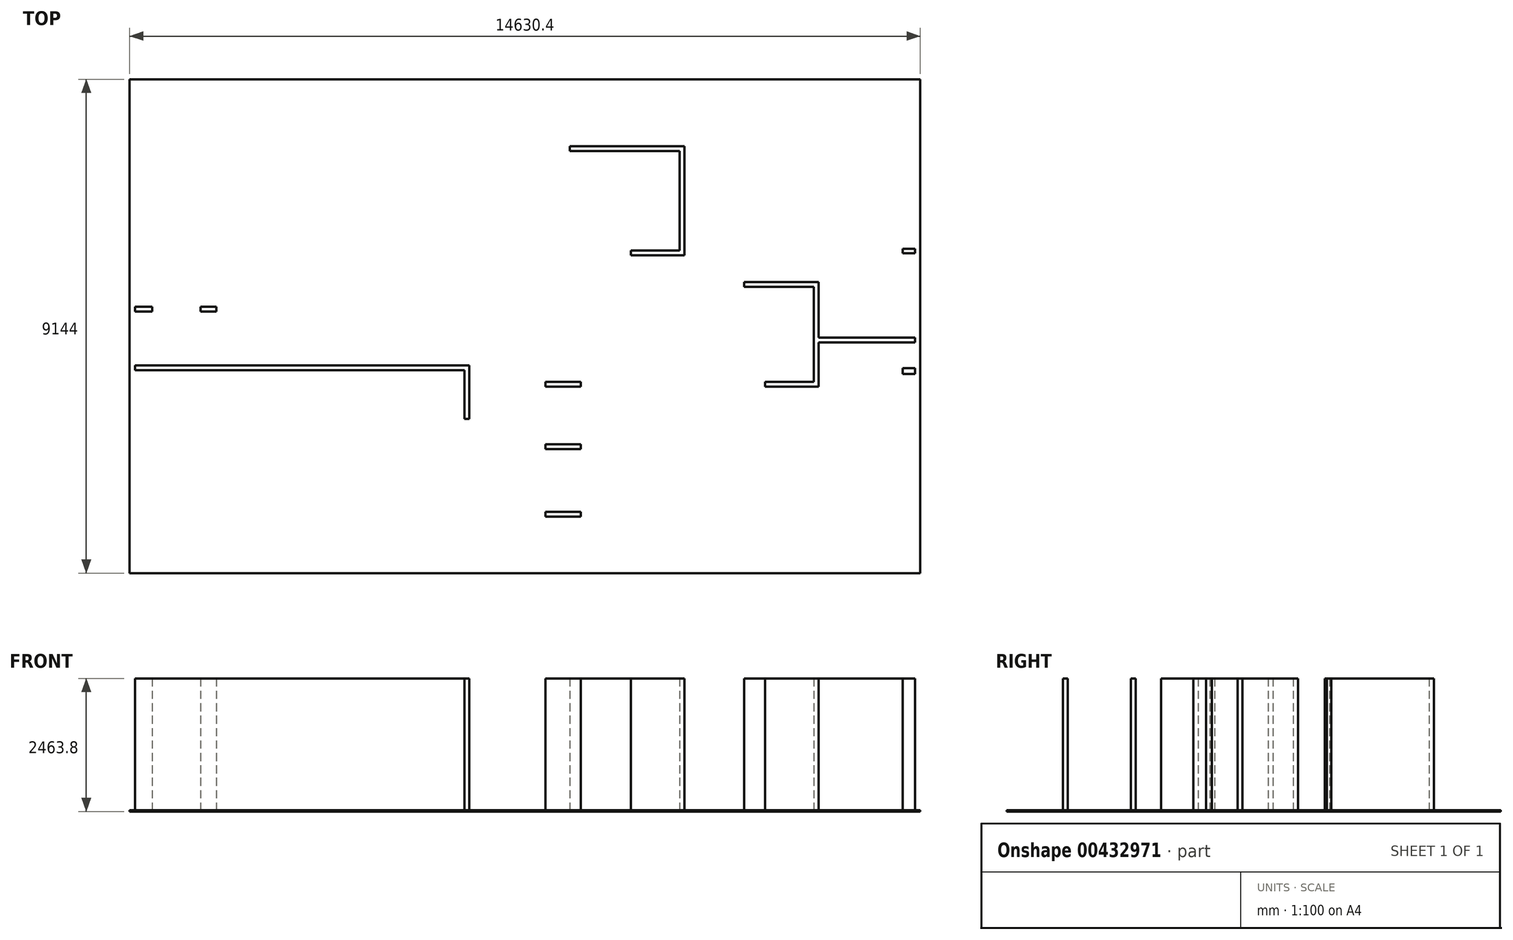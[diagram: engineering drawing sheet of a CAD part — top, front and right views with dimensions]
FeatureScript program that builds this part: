
annotation { "Feature Type Name" : "Feature", "Feature Type Description" : "" }
export const myFeature = defineFeature(function(context is Context, id is Id, definition is map)
    precondition{}
    {
        {
            var Q0;
            Q0=qCreatedBy(makeId("Top.planeOp"),FACE);
            var sketch = newSketch(context, id + "F0", { "sketchPlane" : qUnion([Q0])});
            skLineSegment(sketch, "E0.bottom", {"start": v(-7315.2, -4572) * mm, "end": v(7315.2, -4572) * mm});
            skLineSegment(sketch, "E0.top", {"start": v(-7315.2, 4572) * mm, "end": v(7315.2, 4572) * mm});
            skLineSegment(sketch, "E0.left", {"start": v(-7315.2, -4572) * mm, "end": v(-7315.2, 4572) * mm});
            skLineSegment(sketch, "E0.right", {"start": v(7315.2, -4572) * mm, "end": v(7315.2, 4572) * mm});
            skPoint(sketch, "E0.middle", {"position": v(0, 0) * mm});
            skSolve(sketch);
        }
        {
            var Q0;
            Q0 = qSketchRegion(id + "F0", true);
            extrude(context, id + "F1", {"entities" : qUnion([Q0]), "depth" : 25.4 * mm});
        }
        {
            var Q0;
            Q0=makeQuery(id+"F1.opExtrude","CAP_FACE",FACE,{"disambiguationData":[OSD([sQuery(id+"F0.wireOp",EDGE,"E0.bottom"),sQuery(id+"F0.wireOp",EDGE,"E0.top"),sQuery(id+"F0.wireOp",EDGE,"E0.left"),sQuery(id+"F0.wireOp",EDGE,"E0.right")])],"isStart":false});
            var sketch = newSketch(context, id + "F2", { "sketchPlane" : qUnion([Q0])});
            skLineSegment(sketch, "E1.0", {"start": v(-7216.78, 4473.58) * mm, "end": v(7216.77, 4473.58) * mm});
            skLineSegment(sketch, "E1.1", {"start": v(-7216.78, -4473.58) * mm, "end": v(-7216.78, 4473.58) * mm});
            skLineSegment(sketch, "E1.2", {"start": v(-7216.78, -4473.58) * mm, "end": v(7216.78, -4473.58) * mm});
            skLineSegment(sketch, "E1.3", {"start": v(7216.78, -4473.58) * mm, "end": v(7216.77, 4473.58) * mm});
            skLineSegment(sketch, "E2.bottom", {"start": v(-7216.78, -815.98) * mm, "end": v(-1120.78, -815.98) * mm});
            skLineSegment(sketch, "E2.top", {"start": v(-7216.78, -727.08) * mm, "end": v(-1120.78, -727.08) * mm});
            skLineSegment(sketch, "E2.left", {"start": v(-7216.78, -815.98) * mm, "end": v(-7216.78, -727.08) * mm});
            skLineSegment(sketch, "E2.right", {"start": v(-1120.78, -815.98) * mm, "end": v(-1120.78, -727.08) * mm});
            skLineSegment(sketch, "E3.bottom", {"start": v(-1120.78, -727.08) * mm, "end": v(-1031.88, -727.08) * mm});
            skLineSegment(sketch, "E3.top", {"start": v(-1120.78, -1715.42) * mm, "end": v(-1031.87, -1715.42) * mm});
            skLineSegment(sketch, "E3.left", {"start": v(-1120.78, -727.08) * mm, "end": v(-1120.78, -1715.42) * mm});
            skLineSegment(sketch, "E3.right", {"start": v(-1031.88, -727.08) * mm, "end": v(-1031.87, -1715.42) * mm});
            skLineSegment(sketch, "E4.bottom", {"start": v(-1031.87, -4473.58) * mm, "end": v(-1120.77, -4473.58) * mm});
            skLineSegment(sketch, "E4.top", {"start": v(-1031.87, -2919.2) * mm, "end": v(-1120.78, -2919.2) * mm});
            skLineSegment(sketch, "E4.left", {"start": v(-1031.87, -4473.58) * mm, "end": v(-1031.87, -2919.2) * mm});
            skLineSegment(sketch, "E4.right", {"start": v(-1120.77, -4473.58) * mm, "end": v(-1120.78, -2919.2) * mm});
            skLineSegment(sketch, "E5.bottom", {"start": v(-7216.78, 356.82) * mm, "end": v(-6898.68, 356.82) * mm});
            skLineSegment(sketch, "E5.top", {"start": v(-7216.78, 267.92) * mm, "end": v(-6898.68, 267.92) * mm});
            skLineSegment(sketch, "E5.left", {"start": v(-7216.78, 356.82) * mm, "end": v(-7216.78, 267.92) * mm});
            skLineSegment(sketch, "E5.right", {"start": v(-6898.68, 356.82) * mm, "end": v(-6898.68, 267.92) * mm});
            skLineSegment(sketch, "E6.bottom", {"start": v(-6003.33, 356.82) * mm, "end": v(-5713.3, 356.82) * mm});
            skLineSegment(sketch, "E6.top", {"start": v(-6003.33, 267.92) * mm, "end": v(-5713.3, 267.92) * mm});
            skLineSegment(sketch, "E6.left", {"start": v(-6003.33, 356.82) * mm, "end": v(-6003.33, 267.92) * mm});
            skLineSegment(sketch, "E6.right", {"start": v(-5713.3, 356.82) * mm, "end": v(-5713.3, 267.92) * mm});
            skLineSegment(sketch, "E7.bottom", {"start": v(-5864.23, -727.08) * mm, "end": v(-5775.33, -727.08) * mm});
            skLineSegment(sketch, "E7.top", {"start": v(-5864.23, 267.92) * mm, "end": v(-5775.33, 267.92) * mm});
            skLineSegment(sketch, "E7.left", {"start": v(-5864.23, -727.08) * mm, "end": v(-5864.23, 267.92) * mm});
            skLineSegment(sketch, "E7.right", {"start": v(-5775.33, -727.08) * mm, "end": v(-5775.33, 267.92) * mm});
            skLineSegment(sketch, "E8.bottom", {"start": v(-3994.28, -727.08) * mm, "end": v(-3905.38, -727.08) * mm});
            skLineSegment(sketch, "E8.top", {"start": v(-3994.28, 202.17) * mm, "end": v(-3905.38, 202.17) * mm});
            skLineSegment(sketch, "E8.left", {"start": v(-3994.28, -727.08) * mm, "end": v(-3994.28, 202.17) * mm});
            skLineSegment(sketch, "E8.right", {"start": v(-3905.38, -727.08) * mm, "end": v(-3905.38, 202.17) * mm});
            skLineSegment(sketch, "E9.bottom", {"start": v(1031.88, -4473.58) * mm, "end": v(942.97, -4473.58) * mm});
            skLineSegment(sketch, "E9.top", {"start": v(1031.88, -3530.3) * mm, "end": v(942.97, -3530.3) * mm});
            skLineSegment(sketch, "E9.left", {"start": v(1031.88, -4473.58) * mm, "end": v(1031.88, -3530.3) * mm});
            skLineSegment(sketch, "E9.right", {"start": v(942.97, -4473.58) * mm, "end": v(942.97, -3530.3) * mm});
            skLineSegment(sketch, "E10.bottom", {"start": v(1031.88, -3530.3) * mm, "end": v(380.54, -3530.3) * mm});
            skLineSegment(sketch, "E10.top", {"start": v(1031.88, -3441.4) * mm, "end": v(380.54, -3441.4) * mm});
            skLineSegment(sketch, "E10.left", {"start": v(1031.88, -3530.3) * mm, "end": v(1031.88, -3441.4) * mm});
            skLineSegment(sketch, "E10.right", {"start": v(380.54, -3530.3) * mm, "end": v(380.54, -3441.4) * mm});
            skLineSegment(sketch, "E11.bottom", {"start": v(4168.78, -4473.58) * mm, "end": v(4079.87, -4473.58) * mm});
            skLineSegment(sketch, "E11.top", {"start": v(4168.78, -1279.36) * mm, "end": v(4079.87, -1279.36) * mm});
            skLineSegment(sketch, "E11.left", {"start": v(4168.78, -4473.58) * mm, "end": v(4168.78, -1279.36) * mm});
            skLineSegment(sketch, "E11.right", {"start": v(4079.87, -4473.58) * mm, "end": v(4079.87, -1279.36) * mm});
            skLineSegment(sketch, "E12", {"start": v(0, -4473.58) * mm, "end": v(0, 0) * mm, "construction": true});
            skLineSegment(sketch, "E13.bottom", {"start": v(1031.88, -3441.4) * mm, "end": v(942.97, -3441.4) * mm});
            skLineSegment(sketch, "E13.top", {"start": v(1031.87, -2277.18) * mm, "end": v(942.97, -2277.18) * mm});
            skLineSegment(sketch, "E13.left", {"start": v(1031.88, -3441.4) * mm, "end": v(1031.88, -2277.18) * mm});
            skLineSegment(sketch, "E13.right", {"start": v(942.97, -3441.4) * mm, "end": v(942.97, -2277.18) * mm});
            skLineSegment(sketch, "E14.bottom", {"start": v(1031.87, -2277.18) * mm, "end": v(380.54, -2277.18) * mm});
            skLineSegment(sketch, "E14.top", {"start": v(1031.87, -2188.28) * mm, "end": v(380.54, -2188.28) * mm});
            skLineSegment(sketch, "E14.left", {"start": v(1031.87, -2277.18) * mm, "end": v(1031.87, -2188.28) * mm});
            skLineSegment(sketch, "E14.right", {"start": v(380.54, -2277.18) * mm, "end": v(380.54, -2188.28) * mm});
            skLineSegment(sketch, "E15.bottom", {"start": v(380.54, -2188.28) * mm, "end": v(458.38, -2188.28) * mm});
            skLineSegment(sketch, "E15.top", {"start": v(380.54, -1120.78) * mm, "end": v(458.38, -1120.78) * mm});
            skLineSegment(sketch, "E15.left", {"start": v(380.54, -2188.28) * mm, "end": v(380.54, -1120.78) * mm});
            skLineSegment(sketch, "E15.right", {"start": v(458.38, -2188.28) * mm, "end": v(458.38, -1120.78) * mm});
            skLineSegment(sketch, "E16.bottom", {"start": v(380.54, -1120.78) * mm, "end": v(1031.88, -1120.78) * mm});
            skLineSegment(sketch, "E16.top", {"start": v(380.54, -1031.87) * mm, "end": v(1031.88, -1031.87) * mm});
            skLineSegment(sketch, "E16.left", {"start": v(380.54, -1120.78) * mm, "end": v(380.54, -1031.87) * mm});
            skLineSegment(sketch, "E16.right", {"start": v(1031.88, -1120.78) * mm, "end": v(1031.88, -1031.87) * mm});
            skLineSegment(sketch, "E17.bottom", {"start": v(7216.78, 1432.79) * mm, "end": v(6987.65, 1432.79) * mm});
            skLineSegment(sketch, "E17.top", {"start": v(7216.78, 1350.5) * mm, "end": v(6987.65, 1350.5) * mm});
            skLineSegment(sketch, "E17.left", {"start": v(7216.78, 1432.79) * mm, "end": v(7216.78, 1350.5) * mm});
            skLineSegment(sketch, "E17.right", {"start": v(6987.65, 1432.79) * mm, "end": v(6987.65, 1350.5) * mm});
            skLineSegment(sketch, "E18.bottom", {"start": v(7216.78, -777.08) * mm, "end": v(6987.65, -777.08) * mm});
            skLineSegment(sketch, "E18.top", {"start": v(7216.78, -884.11) * mm, "end": v(6987.65, -884.11) * mm});
            skLineSegment(sketch, "E18.left", {"start": v(7216.78, -777.08) * mm, "end": v(7216.78, -884.11) * mm});
            skLineSegment(sketch, "E18.right", {"start": v(6987.65, -777.08) * mm, "end": v(6987.65, -884.11) * mm});
            skLineSegment(sketch, "E19.bottom", {"start": v(7216.78, -209.65) * mm, "end": v(5437.04, -209.65) * mm});
            skLineSegment(sketch, "E19.top", {"start": v(7216.78, -298.55) * mm, "end": v(5437.04, -298.55) * mm});
            skLineSegment(sketch, "E19.left", {"start": v(7216.78, -209.65) * mm, "end": v(7216.78, -298.55) * mm});
            skLineSegment(sketch, "E19.right", {"start": v(5437.04, -209.65) * mm, "end": v(5437.04, -298.55) * mm});
            skLineSegment(sketch, "E20.bottom", {"start": v(5348.14, 815.98) * mm, "end": v(5437.04, 815.98) * mm});
            skLineSegment(sketch, "E20.top", {"start": v(5348.14, -1120.77) * mm, "end": v(5437.04, -1120.77) * mm});
            skLineSegment(sketch, "E20.left", {"start": v(5348.14, 815.98) * mm, "end": v(5348.14, -1120.77) * mm});
            skLineSegment(sketch, "E20.right", {"start": v(5437.04, 815.98) * mm, "end": v(5437.04, -1120.77) * mm});
            skLineSegment(sketch, "E21.bottom", {"start": v(5348.14, -1120.77) * mm, "end": v(4444.86, -1120.77) * mm});
            skLineSegment(sketch, "E21.top", {"start": v(5348.14, -1031.87) * mm, "end": v(4444.86, -1031.87) * mm});
            skLineSegment(sketch, "E21.left", {"start": v(5348.14, -1120.77) * mm, "end": v(5348.14, -1031.87) * mm});
            skLineSegment(sketch, "E21.right", {"start": v(4444.86, -1120.77) * mm, "end": v(4444.86, -1031.87) * mm});
            skLineSegment(sketch, "E22.bottom", {"start": v(5348.14, 815.98) * mm, "end": v(4058.9, 815.98) * mm});
            skLineSegment(sketch, "E22.top", {"start": v(5348.14, 727.08) * mm, "end": v(4058.9, 727.08) * mm});
            skLineSegment(sketch, "E22.left", {"start": v(5348.14, 815.98) * mm, "end": v(5348.14, 727.08) * mm});
            skLineSegment(sketch, "E22.right", {"start": v(4058.9, 815.98) * mm, "end": v(4058.9, 727.07) * mm});
            skLineSegment(sketch, "E23.bottom", {"start": v(2860.67, 3332.3) * mm, "end": v(2949.57, 3332.3) * mm});
            skLineSegment(sketch, "E23.top", {"start": v(2860.68, 1313.63) * mm, "end": v(2949.58, 1313.63) * mm});
            skLineSegment(sketch, "E23.left", {"start": v(2860.67, 3332.3) * mm, "end": v(2860.68, 1313.63) * mm});
            skLineSegment(sketch, "E23.right", {"start": v(2949.57, 3332.3) * mm, "end": v(2949.58, 1313.63) * mm});
            skLineSegment(sketch, "E24.bottom", {"start": v(2860.67, 3332.3) * mm, "end": v(831.91, 3332.3) * mm});
            skLineSegment(sketch, "E24.top", {"start": v(2860.67, 3243.4) * mm, "end": v(831.91, 3243.4) * mm});
            skLineSegment(sketch, "E24.left", {"start": v(2860.67, 3332.3) * mm, "end": v(2860.67, 3243.4) * mm});
            skLineSegment(sketch, "E24.right", {"start": v(831.91, 3332.3) * mm, "end": v(831.91, 3243.4) * mm});
            skLineSegment(sketch, "E25.bottom", {"start": v(831.91, 3332.3) * mm, "end": v(920.81, 3332.3) * mm});
            skLineSegment(sketch, "E25.top", {"start": v(831.91, 4473.58) * mm, "end": v(920.81, 4473.58) * mm});
            skLineSegment(sketch, "E25.left", {"start": v(831.91, 3332.3) * mm, "end": v(831.91, 4473.58) * mm});
            skLineSegment(sketch, "E25.right", {"start": v(920.81, 3332.3) * mm, "end": v(920.81, 4473.58) * mm});
            skLineSegment(sketch, "E26.bottom", {"start": v(2860.68, 1313.63) * mm, "end": v(1957.6, 1313.63) * mm});
            skLineSegment(sketch, "E26.top", {"start": v(2860.68, 1402.53) * mm, "end": v(1957.6, 1402.53) * mm});
            skLineSegment(sketch, "E26.left", {"start": v(2860.68, 1313.63) * mm, "end": v(2860.68, 1402.53) * mm});
            skLineSegment(sketch, "E26.right", {"start": v(1957.6, 1313.63) * mm, "end": v(1957.6, 1402.53) * mm});
            skLineSegment(sketch, "E27.bottom", {"start": v(831.91, 3243.4) * mm, "end": v(920.81, 3243.4) * mm});
            skLineSegment(sketch, "E27.top", {"start": v(831.91, 1313.63) * mm, "end": v(920.81, 1313.63) * mm});
            skLineSegment(sketch, "E27.left", {"start": v(831.91, 3243.4) * mm, "end": v(831.91, 1313.63) * mm});
            skLineSegment(sketch, "E27.right", {"start": v(920.81, 3243.4) * mm, "end": v(920.81, 1313.63) * mm});
            skSolve(sketch);
        }
        {
            var Q0;
            {var subQ6=sQuery(id+"F2.wireOp",EDGE,"E2.bottom");Q0=makeQuery(id+"F2.imprint","IMPRINT",FACE,{"disambiguationData":[TD([[makeQuery(id+"F2.imprint","IMPRINT",EDGE,{"derivedFrom":subQ6}),1.0]])]});}
            var Q1;
            {var subQ3=sQuery(id+"F2.wireOp",EDGE,"E3.bottom");Q1=makeQuery(id+"F2.imprint","IMPRINT",FACE,{"disambiguationData":[TD([[makeQuery(id+"F2.imprint","IMPRINT",EDGE,{"derivedFrom":subQ3}),-1.0]])]});}
            var Q2;
            Q2=makeQuery(id+"F2.imprint","IMPRINT",FACE,{"disambiguationData":[TD([[makeQuery(id+"F2.imprint","IMPRINT",EDGE,{"derivedFrom":sQuery(id+"F2.wireOp",EDGE,"E4.bottom")}),-1.0]])]});
            var Q3;
            Q3=makeQuery(id+"F2.imprint","IMPRINT",FACE,{"disambiguationData":[TD([[makeQuery(id+"F2.imprint","IMPRINT",EDGE,{"derivedFrom":sQuery(id+"F2.wireOp",EDGE,"E9.bottom")}),-1.0]])]});
            var Q4;
            Q4=makeQuery(id+"F2.imprint","IMPRINT",FACE,{"disambiguationData":[TD([[makeQuery(id+"F2.imprint","IMPRINT",EDGE,{"derivedFrom":sQuery(id+"F2.wireOp",EDGE,"E10.top")}),1.0]])]});
            var Q5;
            Q5=makeQuery(id+"F2.imprint","IMPRINT",FACE,{"disambiguationData":[TD([[makeQuery(id+"F2.imprint","IMPRINT",EDGE,{"derivedFrom":sQuery(id+"F2.wireOp",EDGE,"E8.bottom")}),1.0]])]});
            var Q6;
            Q6=makeQuery(id+"F2.imprint","IMPRINT",FACE,{"disambiguationData":[TD([[makeQuery(id+"F2.imprint","IMPRINT",EDGE,{"derivedFrom":sQuery(id+"F2.wireOp",EDGE,"E7.bottom")}),1.0]])]});
            var Q7;
            Q7=makeQuery(id+"F2.imprint","IMPRINT",FACE,{"disambiguationData":[TD([[makeQuery(id+"F2.imprint","IMPRINT",EDGE,{"derivedFrom":sQuery(id+"F2.wireOp",EDGE,"E6.bottom")}),-1.0]])]});
            var Q8;
            Q8=makeQuery(id+"F2.imprint","IMPRINT",FACE,{"disambiguationData":[TD([[makeQuery(id+"F2.imprint","IMPRINT",EDGE,{"derivedFrom":sQuery(id+"F2.wireOp",EDGE,"E5.bottom")}),-1.0]])]});
            var Q9;
            Q9=makeQuery(id+"F2.imprint","IMPRINT",FACE,{"disambiguationData":[TD([[makeQuery(id+"F2.imprint","IMPRINT",EDGE,{"derivedFrom":sQuery(id+"F2.wireOp",EDGE,"E13.bottom")}),-1.0]])]});
            var Q10;
            Q10=makeQuery(id+"F2.imprint","IMPRINT",FACE,{"disambiguationData":[TD([[makeQuery(id+"F2.imprint","IMPRINT",EDGE,{"derivedFrom":sQuery(id+"F2.wireOp",EDGE,"E14.top")}),1.0]])]});
            var Q11;
            Q11=makeQuery(id+"F2.imprint","IMPRINT",FACE,{"disambiguationData":[TD([[makeQuery(id+"F2.imprint","IMPRINT",EDGE,{"derivedFrom":sQuery(id+"F2.wireOp",EDGE,"E16.top")}),-1.0]])]});
            var Q12;
            Q12=makeQuery(id+"F2.imprint","IMPRINT",FACE,{"disambiguationData":[TD([[makeQuery(id+"F2.imprint","IMPRINT",EDGE,{"derivedFrom":sQuery(id+"F2.wireOp",EDGE,"E15.bottom")}),1.0]])]});
            var Q13;
            Q13=makeQuery(id+"F2.imprint","IMPRINT",FACE,{"disambiguationData":[TD([[makeQuery(id+"F2.imprint","IMPRINT",EDGE,{"derivedFrom":sQuery(id+"F2.wireOp",EDGE,"E11.bottom")}),-1.0]])]});
            var Q14;
            Q14=makeQuery(id+"F2.imprint","IMPRINT",FACE,{"disambiguationData":[TD([[makeQuery(id+"F2.imprint","IMPRINT",EDGE,{"derivedFrom":sQuery(id+"F2.wireOp",EDGE,"E21.bottom")}),-1.0]])]});
            var Q15;
            {var subQ0=sQuery(id+"F2.wireOp",EDGE,"E19.bottom");Q15=makeQuery(id+"F2.imprint","IMPRINT",FACE,{"disambiguationData":[TD([[makeQuery(id+"F2.imprint","IMPRINT",EDGE,{"derivedFrom":subQ0}),1.0]])]});}
            var Q16;
            Q16=makeQuery(id+"F2.imprint","IMPRINT",FACE,{"disambiguationData":[TD([[makeQuery(id+"F2.imprint","IMPRINT",EDGE,{"derivedFrom":sQuery(id+"F2.wireOp",EDGE,"E18.bottom")}),1.0]])]});
            var Q17;
            {var subQ7=sQuery(id+"F2.wireOp",EDGE,"E2.left");Q17=makeQuery(id+"F2.imprint","IMPRINT",FACE,{"disambiguationData":[TD([[makeQuery(id+"F2.imprint","IMPRINT",EDGE,{"derivedFrom":subQ7}),1.0]])]});}
            var Q18;
            Q18=makeQuery(id+"F2.imprint","IMPRINT",FACE,{"disambiguationData":[TD([[makeQuery(id+"F2.imprint","IMPRINT",EDGE,{"derivedFrom":sQuery(id+"F2.wireOp",EDGE,"E25.bottom")}),1.0]])]});
            var Q19;
            Q19=makeQuery(id+"F2.imprint","IMPRINT",FACE,{"disambiguationData":[TD([[makeQuery(id+"F2.imprint","IMPRINT",EDGE,{"derivedFrom":sQuery(id+"F2.wireOp",EDGE,"E24.bottom")}),1.0]])]});
            var Q20;
            Q20=makeQuery(id+"F2.imprint","IMPRINT",FACE,{"disambiguationData":[TD([[makeQuery(id+"F2.imprint","IMPRINT",EDGE,{"derivedFrom":sQuery(id+"F2.wireOp",EDGE,"E23.bottom")}),-1.0]])]});
            var Q21;
            Q21=makeQuery(id+"F2.imprint","IMPRINT",FACE,{"disambiguationData":[TD([[makeQuery(id+"F2.imprint","IMPRINT",EDGE,{"derivedFrom":sQuery(id+"F2.wireOp",EDGE,"E26.bottom")}),-1.0]])]});
            var Q22;
            Q22=makeQuery(id+"F2.imprint","IMPRINT",FACE,{"disambiguationData":[TD([[makeQuery(id+"F2.imprint","IMPRINT",EDGE,{"derivedFrom":sQuery(id+"F2.wireOp",EDGE,"E27.bottom")}),-1.0]])]});
            var Q23;
            {var subQ2=sQuery(id+"F2.wireOp",EDGE,"E20.bottom");Q23=makeQuery(id+"F2.imprint","IMPRINT",FACE,{"disambiguationData":[TD([[makeQuery(id+"F2.imprint","IMPRINT",EDGE,{"derivedFrom":subQ2}),-1.0]])]});}
            var Q24;
            Q24=makeQuery(id+"F2.imprint","IMPRINT",FACE,{"disambiguationData":[TD([[makeQuery(id+"F2.imprint","IMPRINT",EDGE,{"derivedFrom":sQuery(id+"F2.wireOp",EDGE,"E22.bottom")}),1.0]])]});
            var Q25;
            Q25=makeQuery(id+"F2.imprint","IMPRINT",FACE,{"disambiguationData":[TD([[makeQuery(id+"F2.imprint","IMPRINT",EDGE,{"derivedFrom":sQuery(id+"F2.wireOp",EDGE,"E17.bottom")}),1.0]])]});
            extrude(context, id + "F3", {"entities" : qUnion([Q0, Q1, Q2, Q3, Q4, Q5, Q6, Q7, Q8, Q9, Q10, Q11, Q12, Q13, Q14, Q15, Q16, Q17, Q18, Q19, Q20, Q21, Q22, Q23, Q24, Q25]), "depth" : 2438.4 * mm});
        }
    });
